# Revit family: 05-7641-14-14
name_source: partatom
category: Luminarias
revit_build: Autodesk Revit 2017 (Build: 20160225_1515(x64)
units: mm (PartAtom-declared; Revit-internal decimal feet)

## family parameters
Anfitrión = Cara
Compartido = Sí
Corte con vacíos al cargar = No
Cota de conector redondo = Diámetro de uso
Número OmniClass = 23.80.70.00
Origen de luz = No
Punto de cálculo de habitación = No
Tipo de pieza = Normal
Título OmniClass = Lighting

## types (1)
- 05-7641-14-14
    Acabado = Blanc, Arenat
    CRI = 80
    Carga aparente = 0 VA
    Catálogo = Decorative
    CodigoGubimclass = 50.60.50.20
    CodigoOmniclass = 21-04 50 40
    CodigoUniclass2015 = EF_70_80
    CodigoUniformat2010 = D5040
    DescripcionGubimclass = Iluminación interior
    DescripcionOmniclass = Lighting
    DescripcionUniclass2015 = Lighting
    DescripcionUniformat2010 = Lighting
    EAN13 = 8435526868803
    Eficiencia energética = LED A++
    Elevación por defecto = 1000 mm  [stored 3.28084 ft]
    Etiqueta V/f = 100-240V/50-60Hz
    Fabricante = LEDS C4
    Familia = Ges Deco Round ø150mm
    FechaVersion = Creada: 21/07/2021
    Ficha = https://files.leds-c4.com
    Fotometría = https://files.leds-c4.com
    IMC = https://files.leds-c4.com
    IP = IP20
    IfcExportAs = IfcLightFixture
IfcLightFixture
    IfcExportType = NOTDEFINED
    Imagen web = https://files.leds-c4.com
    LDT = https://files.leds-c4.com
    Lumenes reales (lm) = 386
    Material = Acer, Guix, Acrílic
    Peso neto (KG) = 0.72
    Pluma comercial = https://files.leds-c4.com
    Producto descatalogado = Catalogado
    Referencia = 05-7641-14-14
    Temperatura color led (K) = Blanc càlid - 3000K
    Tender text (Castellano) = LEDS C4
Ges Deco Round ø150mm
05-7641-14-14

Aplic d'ús interior per il·luminar cap amunt i cap avall 

Sense cargols a la vista. Òptim preu-rendiment. Òptim confort visual. Efecte de llum indirecte. Alta durabilitat per a ús intensiu. Material de l'estructura: Acer, Guix. Acabat estructura: Blanc. Material del difusor: Acrílic. Acabat difusor: Arenat. Garantia: 5 Anys.

Pes net del producte (Kg): 0.72
Amplada o diàmetre del producte (mm): 150
Alçada del producte (mm): 46

Classe 1. IP: IP20. LED. Nº de portalàmpades o Leds: 30. Marca del Driver: HEP. Potència màxima de la font de llum: 3W. Temperatura de color: 3000K. Índex de reproducció cromàtica: 80. Steps Mac Adam: 3. Diàmetre màxim de la bombeta que admet la lluminària: 50.000h L80B20. UGR: 20.0. Risc fotobiològic: RG0. Flux real (lm): 386. Lm / W reals: 97. Rang de voltatge / freqüència: 100-277/50-60Hz. Voltatge: 3. Equip inclòs: Si, electrònic. Potència total: 4. Factor de potència: 0.50. Equip regulable inclòs: ON-OFF.
    Tender text (English) = LEDS C4
Ges Deco Round ø150mm
05-7641-14-14

Wall fixture for indoor use. 

For uplighting and downlighting. No visible screws. Optimum price-performance. Optimum visual comfort. Indirect light effect. High durability for intensive use. Structure material: Steel, Plaster. Structure finish: White. Diffuser material: Acrylic. Diffuser finish: Sandblasted. Warranty: 5 Years.

Product net weight (Kg): 0.72
Product width or diameter (mm): 150
Product height (mm): 46

Class 1. IP: IP20. LED. No. of lampholders or LEDs: 30. Driver brand: HEP. Maximum power of light source: 3W. Colour temperature: 3000K. Colour rendering index: 80. MacAdam Steps: 3. Maximum diameter of luminaire bulb: 50.000h L80B20. UGR: 20.0. Photobiological risk: RG0. Real flux (lm): 386. Real lm/W: 97. Voltage / frequency range: 100-277/50-60Hz. Voltage: 3. Equipment included: Yes, electronic. Total power: 4. Power factor: 0.50. Dimmable equipment included: ON-OFF.
    Tipo = Aplic
    Tipo de regulación = ON-OFF
    Vatios (W) = 4
    Versión = v1

note: [stored X ft] marks values corroborated as IEEE doubles in the binary element streams (Revit-internal decimal feet)
